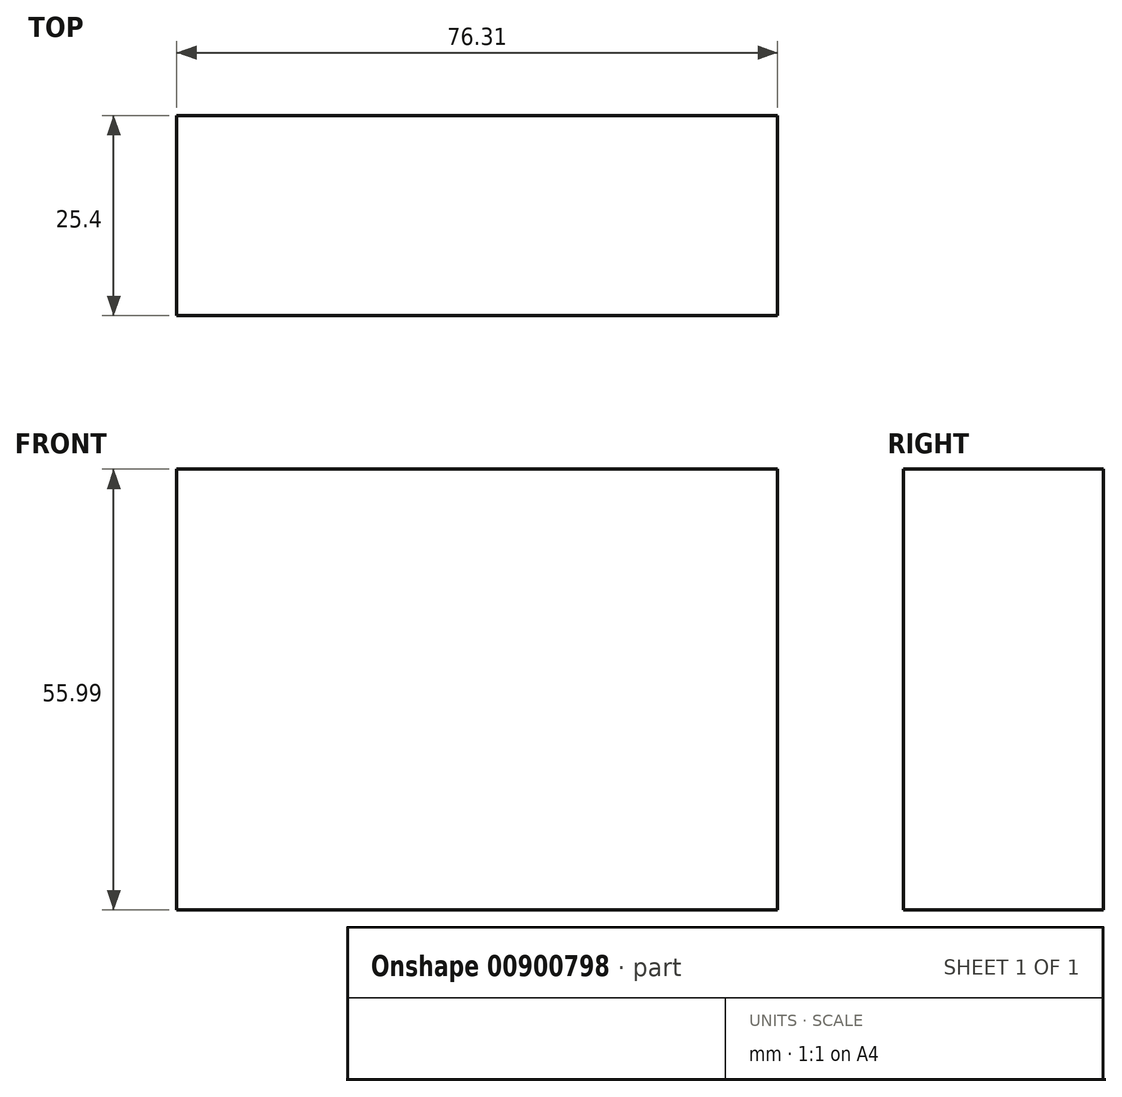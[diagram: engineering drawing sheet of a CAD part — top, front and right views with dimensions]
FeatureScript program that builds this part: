
annotation { "Feature Type Name" : "Feature", "Feature Type Description" : "" }
export const myFeature = defineFeature(function(context is Context, id is Id, definition is map)
    precondition{}
    {
        {
            var Q0;
            Q0=qCreatedBy(makeId("Front.planeOp"),FACE);
            var sketch = newSketch(context, id + "F0", { "sketchPlane" : qUnion([Q0])});
            skLineSegment(sketch, "E0.bottom", {"start": v(0, 0) * mm, "end": v(76.3, 0) * mm});
            skLineSegment(sketch, "E0.top", {"start": v(0, 55.99) * mm, "end": v(76.3, 55.99) * mm});
            skLineSegment(sketch, "E0.left", {"start": v(0, 0) * mm, "end": v(0, 55.99) * mm});
            skLineSegment(sketch, "E0.right", {"start": v(76.3, 0) * mm, "end": v(76.3, 55.99) * mm});
            skSolve(sketch);
        }
        {
            var Q0;
            Q0 = qSketchRegion(id + "F0", true);
            extrude(context, id + "F1", {"entities" : qUnion([Q0]), "depth" : 25.4 * mm, "offsetDistance" : 25.4 * mm});
        }
    });
